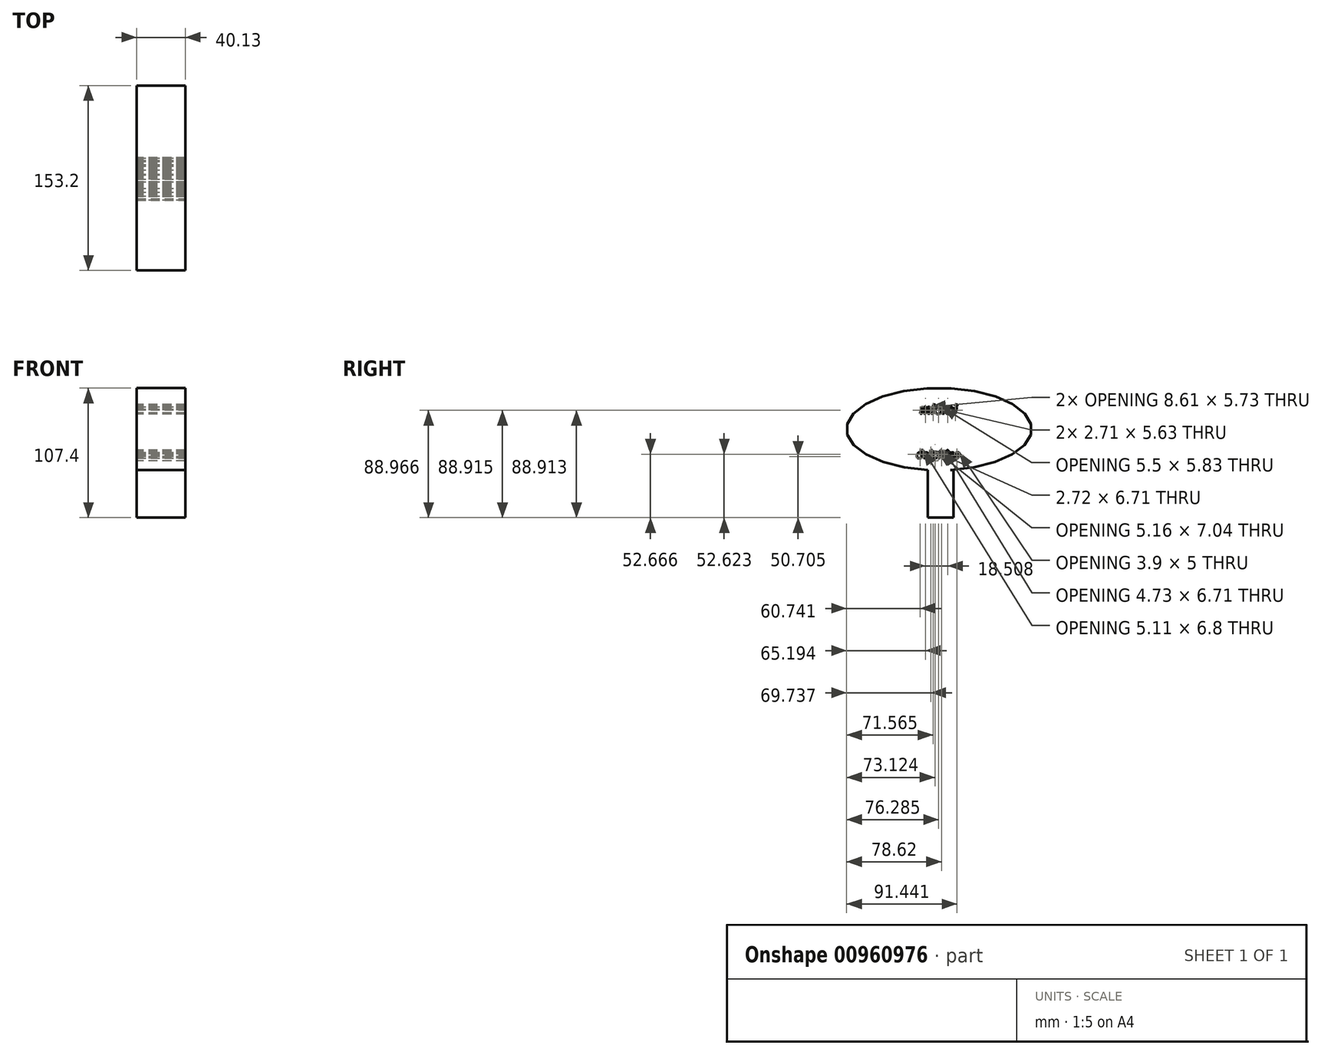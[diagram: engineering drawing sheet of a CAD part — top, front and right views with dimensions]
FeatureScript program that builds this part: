
annotation { "Feature Type Name" : "Feature", "Feature Type Description" : "" }
export const myFeature = defineFeature(function(context is Context, id is Id, definition is map)
    precondition{}
    {
        {
            var Q0;
            Q0=qCreatedBy(makeId("Right.planeOp"),FACE);
            var sketch = newSketch(context, id + "F0", { "sketchPlane" : qUnion([Q0])});
            skEllipse(sketch, "E0", {"center": v(0, 0) * mm, "majorRadius": 76.6 * mm, "minorRadius": 34 * mm, "majorAxis": v(1, 0)});
            skText(sketch, "E1", { "text": "miami", "fontName": "OpenSans-BoldItalic.ttf"});
            skLineSegment(sketch, "E2", {"start": v(-76.6, 0) * mm, "end": v(76.6, 0) * mm});
            skLineSegment(sketch, "E3", {"start": v(-51.83, 6.43) * mm, "end": v(-51.83, -5.85) * mm});
            skLineSegment(sketch, "E4", {"start": v(-36.12, 8.42) * mm, "end": v(-36.12, -7) * mm});
            skLineSegment(sketch, "E5", {"start": v(-31.84, 9) * mm, "end": v(-31.84, -4.14) * mm});
            skLineSegment(sketch, "E6", {"start": v(-22.13, 7) * mm, "end": v(-22.13, -7) * mm});
            skLineSegment(sketch, "E7", {"start": v(-13.56, 4.71) * mm, "end": v(-13.56, -4.14) * mm});
            skLineSegment(sketch, "E8", {"start": v(-5.57, 3.28) * mm, "end": v(-5.57, -7) * mm});
            skLineSegment(sketch, "E9", {"start": v(2.71, 6.43) * mm, "end": v(2.71, -7) * mm});
            skLineSegment(sketch, "E10", {"start": v(9.85, 5.28) * mm, "end": v(9.85, -7) * mm});
            skLineSegment(sketch, "E11", {"start": v(15.56, 3.28) * mm, "end": v(15.56, -9.28) * mm});
            skLineSegment(sketch, "E12", {"start": v(23.85, 4.43) * mm, "end": v(23.85, -4.71) * mm});
            skLineSegment(sketch, "E13", {"start": v(35.84, 6.14) * mm, "end": v(35.84, -3.57) * mm});
            skLineSegment(sketch, "E14", {"start": v(43.26, 6.71) * mm, "end": v(43.26, -3.57) * mm});
            skLineSegment(sketch, "E15", {"start": v(52.69, 5.57) * mm, "end": v(52.69, -3.57) * mm});
            skLineSegment(sketch, "E16", {"start": v(48.98, 5.57) * mm, "end": v(48.98, -3.57) * mm});
            skLineSegment(sketch, "E17", {"start": v(30.7, 5.57) * mm, "end": v(30.7, -7) * mm});
            skLineSegment(sketch, "E18", {"start": v(-26.7, 4.71) * mm, "end": v(-26.7, -7) * mm});
            skLineSegment(sketch, "E19", {"start": v(-17.85, 3.28) * mm, "end": v(-17.85, -7) * mm});
            skLineSegment(sketch, "E20", {"start": v(-46.98, 10.7) * mm, "end": v(-43.84, -5.85) * mm});
            skLineSegment(sketch, "E21.bottom", {"start": v(-9.3, -33.75) * mm, "end": v(11.84, -33.75) * mm});
            skLineSegment(sketch, "E21.top", {"start": v(-9.3, -73.4) * mm, "end": v(11.84, -73.4) * mm});
            skLineSegment(sketch, "E21.left", {"start": v(-9.3, -33.75) * mm, "end": v(-9.3, -73.4) * mm});
            skLineSegment(sketch, "E21.right", {"start": v(11.84, -33.75) * mm, "end": v(11.84, -73.4) * mm});
            skText(sketch, "E22", { "text": "dolphins", "fontName": "OpenSans-BoldItalic.ttf"});
            const initialGuessF0  = {"E1": [-0.0159, 0.0127, 1, 0, 0.00742], "E22": [-0.0188, -0.02409, 1, 0, 0.00636]};
            skSetInitialGuess(sketch, initialGuessF0);
            skSolve(sketch);
        }
        {
            var Q0;
            Q0 = qSketchRegion(id + "F0", true);
            extrude(context, id + "F1", {"entities" : qUnion([Q0]), "depth" : 40.13 * mm, "offsetDistance" : 25.4 * mm});
        }
    });
